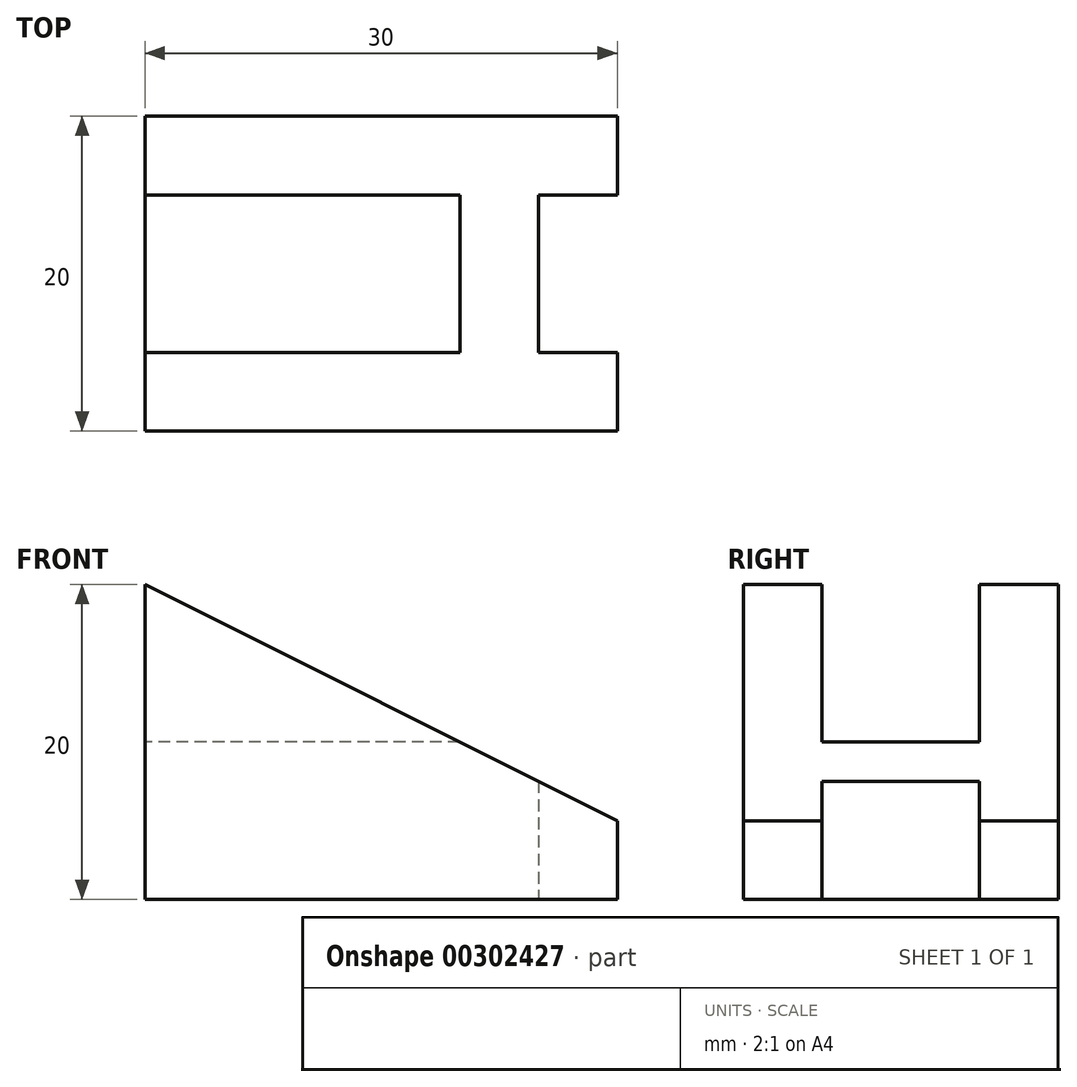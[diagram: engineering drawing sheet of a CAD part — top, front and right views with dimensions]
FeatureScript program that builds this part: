
annotation { "Feature Type Name" : "Feature", "Feature Type Description" : "" }
export const myFeature = defineFeature(function(context is Context, id is Id, definition is map)
    precondition{}
    {
        {
            var Q0;
            Q0=qCreatedBy(makeId("Front.planeOp"),FACE);
            var sketch = newSketch(context, id + "F0", { "sketchPlane" : qUnion([Q0])});
            skLineSegment(sketch, "E0", {"start": v(-15, 20) * mm, "end": v(-15, 0) * mm});
            skLineSegment(sketch, "E1", {"start": v(-15, 0) * mm, "end": v(15, 0) * mm});
            skLineSegment(sketch, "E2", {"start": v(15, 0) * mm, "end": v(15, 5) * mm});
            skLineSegment(sketch, "E3", {"start": v(15, 5) * mm, "end": v(-15, 20) * mm});
            skSolve(sketch);
        }
        {
            var Q0;
            Q0 = qSketchRegion(id + "F0", true);
            extrude(context, id + "F1", {"entities" : qUnion([Q0]), "depth" : 20 * mm});
        }
        {
            var Q0;
            Q0=qCreatedBy(makeId("Top.planeOp"),FACE);
            var sketch = newSketch(context, id + "F2", { "sketchPlane" : qUnion([Q0])});
            skLineSegment(sketch, "E4.bottom", {"start": v(10, -5) * mm, "end": v(15, -5) * mm});
            skLineSegment(sketch, "E4.top", {"start": v(10, -15) * mm, "end": v(15, -15) * mm});
            skLineSegment(sketch, "E4.left", {"start": v(10, -5) * mm, "end": v(10, -15) * mm});
            skLineSegment(sketch, "E4.right", {"start": v(15, -5) * mm, "end": v(15, -15) * mm});
            skSolve(sketch);
        }
        {
            var Q0;
            Q0 = qSketchRegion(id + "F2", true);
            extrude(context, id + "F3", {"entities" : qUnion([Q0]), "operationType" : NewBodyOperationType.REMOVE, "depth" : 25 * mm});
        }
        {
            var Q0;
            Q0=makeQuery(id+"F1.opExtrude","SWEPT_FACE",FACE,{"disambiguationData":[OSD([sQuery(id+"F0.wireOp",EDGE,"E0")])]});
            var sketch = newSketch(context, id + "F4", { "sketchPlane" : qUnion([Q0])});
            skLineSegment(sketch, "E5.bottom", {"start": v(5, 20) * mm, "end": v(15, 20) * mm});
            skLineSegment(sketch, "E5.top", {"start": v(5, 10) * mm, "end": v(15, 10) * mm});
            skLineSegment(sketch, "E5.left", {"start": v(5, 20) * mm, "end": v(5, 10) * mm});
            skLineSegment(sketch, "E5.right", {"start": v(15, 20) * mm, "end": v(15, 10) * mm});
            skSolve(sketch);
        }
        {
            var Q0;
            Q0 = qSketchRegion(id + "F4", true);
            extrude(context, id + "F5", {"entities" : qUnion([Q0]), "operationType" : NewBodyOperationType.REMOVE, "oppositeDirection" : true, "depth" : 25 * mm});
        }
    });
